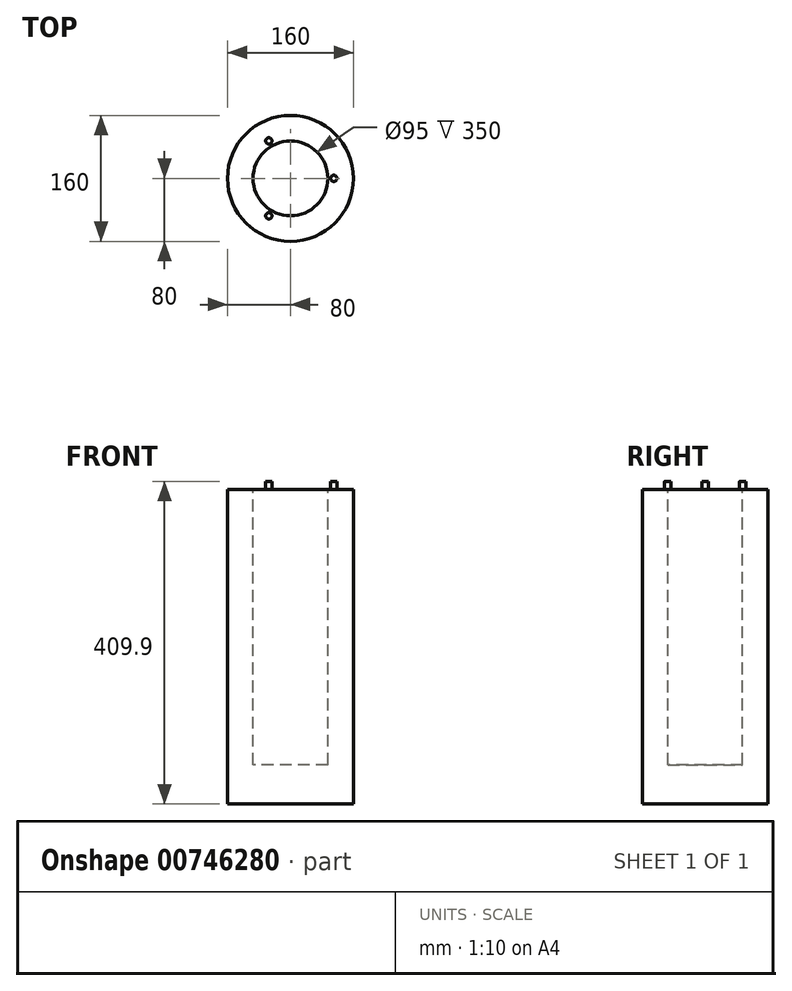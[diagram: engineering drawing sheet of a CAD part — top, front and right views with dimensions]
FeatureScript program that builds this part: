
annotation { "Feature Type Name" : "Feature", "Feature Type Description" : "" }
export const myFeature = defineFeature(function(context is Context, id is Id, definition is map)
    precondition{}
    {
        {
            var Q0;
            Q0=qCreatedBy(makeId("Top.planeOp"),FACE);
            var sketch = newSketch(context, id + "F0", { "sketchPlane" : qUnion([Q0])});
            skCircle(sketch, "E0", {"center": v(0, 0) * mm, "radius": 80 * mm});
            skCircle(sketch, "E1", {"center": v(0, 0) * mm, "radius": 47.5 * mm});
            skCircle(sketch, "E2", {"center": v(0, 0) * mm, "radius": 55 * mm, "construction": true});
            skCircle(sketch, "E3", {"center": v(55, 0) * mm, "radius": 4 * mm});
            skCircle(sketch, "E4.1.0", {"center": v(-27.5, 47.63) * mm, "radius": 4 * mm});
            skCircle(sketch, "E4.2.0", {"center": v(-27.5, -47.63) * mm, "radius": 4 * mm});
            skSolve(sketch);
        }
        {
            var Q0;
            Q0 = qSketchRegion(id + "F0", true);
            var Q1;
            Q1=makeQuery(id+"F0.imprint","IMPRINT",FACE,{"disambiguationData":[TD([[makeQuery(id+"F0.imprint","IMPRINT",EDGE,{"derivedFrom":sQuery(id+"F0.wireOp",EDGE,"E1")}),1.0]])]});
            var Q2;
            Q2=makeQuery(id+"F0.imprint","IMPRINT",FACE,{"disambiguationData":[TD([[makeQuery(id+"F0.imprint","IMPRINT",EDGE,{"derivedFrom":sQuery(id+"F0.wireOp",EDGE,"E4.1.0")}),1.0]])]});
            var Q3;
            Q3=makeQuery(id+"F0.imprint","IMPRINT",FACE,{"disambiguationData":[TD([[makeQuery(id+"F0.imprint","IMPRINT",EDGE,{"derivedFrom":sQuery(id+"F0.wireOp",EDGE,"E3")}),1.0]])]});
            var Q4;
            Q4=makeQuery(id+"F0.imprint","IMPRINT",FACE,{"disambiguationData":[TD([[makeQuery(id+"F0.imprint","IMPRINT",EDGE,{"derivedFrom":sQuery(id+"F0.wireOp",EDGE,"E4.2.0")}),1.0]])]});
            extrude(context, id + "F1", {"entities" : qUnion([Q0, Q1, Q2, Q3, Q4]), "oppositeDirection" : true, "depth" : 400 * mm, "offsetDistance" : 25 * mm});
        }
        {
            var Q0;
            Q0=makeQuery(id+"F0.imprint","IMPRINT",FACE,{"disambiguationData":[TD([[makeQuery(id+"F0.imprint","IMPRINT",EDGE,{"derivedFrom":sQuery(id+"F0.wireOp",EDGE,"E4.2.0")}),1.0]])]});
            var Q1;
            Q1=makeQuery(id+"F0.imprint","IMPRINT",FACE,{"disambiguationData":[TD([[makeQuery(id+"F0.imprint","IMPRINT",EDGE,{"derivedFrom":sQuery(id+"F0.wireOp",EDGE,"E3")}),1.0]])]});
            var Q2;
            Q2=makeQuery(id+"F0.imprint","IMPRINT",FACE,{"disambiguationData":[TD([[makeQuery(id+"F0.imprint","IMPRINT",EDGE,{"derivedFrom":sQuery(id+"F0.wireOp",EDGE,"E4.1.0")}),1.0]])]});
            extrude(context, id + "F2", {"entities" : qUnion([Q0, Q1, Q2]), "operationType" : NewBodyOperationType.ADD, "depth" : 9.9 * mm, "offsetDistance" : 25 * mm});
        }
        {
            var Q0;
            Q0=makeQuery(id+"F0.imprint","IMPRINT",FACE,{"disambiguationData":[TD([[makeQuery(id+"F0.imprint","IMPRINT",EDGE,{"derivedFrom":sQuery(id+"F0.wireOp",EDGE,"E1")}),1.0]])]});
            extrude(context, id + "F3", {"entities" : qUnion([Q0]), "operationType" : NewBodyOperationType.REMOVE, "oppositeDirection" : true, "depth" : 350 * mm, "offsetDistance" : 25 * mm});
        }
    });
